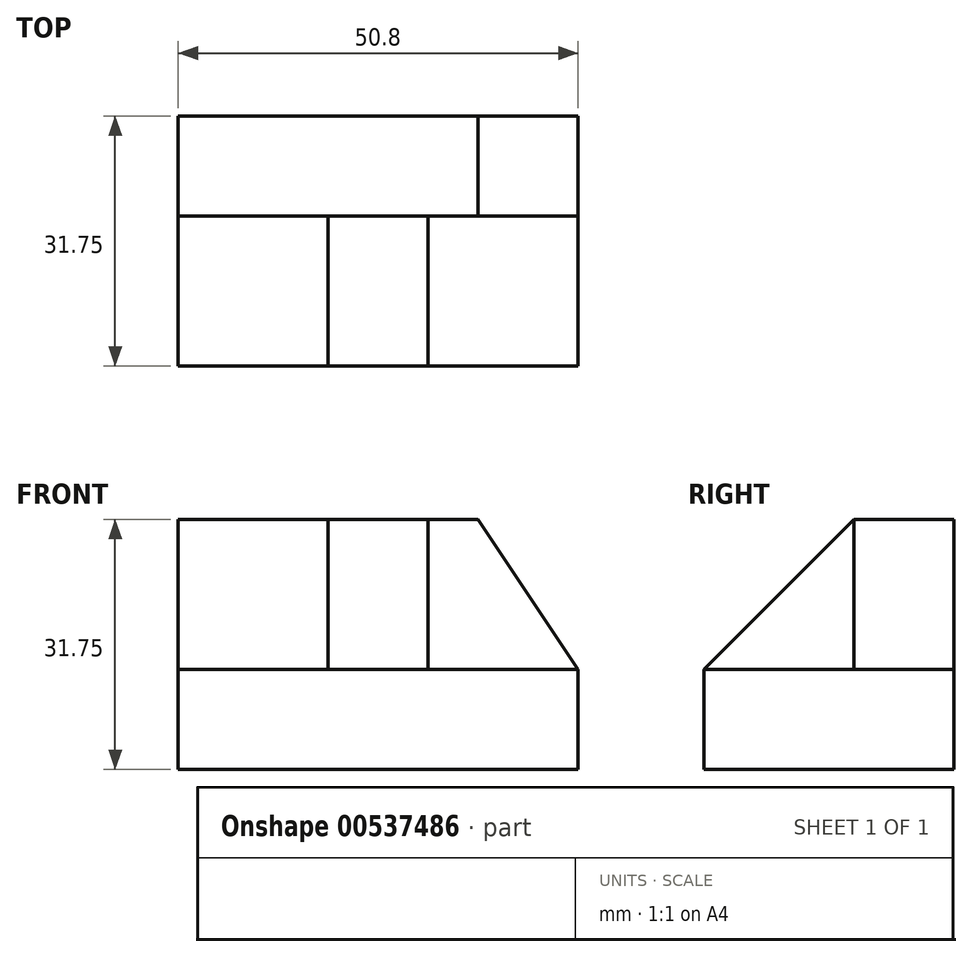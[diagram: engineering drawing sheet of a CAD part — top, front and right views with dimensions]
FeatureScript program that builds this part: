
annotation { "Feature Type Name" : "Feature", "Feature Type Description" : "" }
export const myFeature = defineFeature(function(context is Context, id is Id, definition is map)
    precondition{}
    {
        {
            var Q0;
            Q0=qCreatedBy(makeId("Front.planeOp"),FACE);
            var sketch = newSketch(context, id + "F0", { "sketchPlane" : qUnion([Q0])});
            skLineSegment(sketch, "E0", {"start": v(0, 0) * mm, "end": v(50.8, 0) * mm});
            skLineSegment(sketch, "E1", {"start": v(50.8, 0) * mm, "end": v(50.8, 31.75) * mm});
            skLineSegment(sketch, "E2", {"start": v(50.8, 31.75) * mm, "end": v(0, 31.75) * mm});
            skLineSegment(sketch, "E3", {"start": v(0, 31.75) * mm, "end": v(0, 0) * mm});
            skSolve(sketch);
        }
        {
            var Q0;
            Q0=makeQuery(id+"F0.imprint","IMPRINT",FACE,{"disambiguationData":[TD([[makeQuery(id+"F0.imprint","IMPRINT",EDGE,{"derivedFrom":sQuery(id+"F0.wireOp",EDGE,"E0")}),1.0]])]});
            extrude(context, id + "F1", {"entities" : qUnion([Q0]), "depth" : 31.75 * mm, "offsetDistance" : 25.4 * mm});
        }
        {
            var Q0;
            Q0=makeQuery(id+"F1.opExtrude","SWEPT_FACE",FACE,{"disambiguationData":[OSD([sQuery(id+"F0.wireOp",EDGE,"E1")])]});
            var sketch = newSketch(context, id + "F2", { "sketchPlane" : qUnion([Q0])});
            skLineSegment(sketch, "E4", {"start": v(-31.75, 12.7) * mm, "end": v(-12.7, 12.7) * mm});
            skLineSegment(sketch, "E5", {"start": v(-12.7, 12.7) * mm, "end": v(-12.7, 31.75) * mm});
            skLineSegment(sketch, "E6", {"start": v(-12.7, 31.75) * mm, "end": v(-31.75, 31.75) * mm});
            skLineSegment(sketch, "E7", {"start": v(-31.75, 31.75) * mm, "end": v(-31.75, 12.7) * mm});
            skSolve(sketch);
        }
        {
            var Q0;
            Q0=makeQuery(id+"F2.imprint","IMPRINT",FACE,{"disambiguationData":[TD([[makeQuery(id+"F2.imprint","IMPRINT",EDGE,{"derivedFrom":sQuery(id+"F2.wireOp",EDGE,"E4")}),1.0]])]});
            extrude(context, id + "F3", {"entities" : qUnion([Q0]), "operationType" : NewBodyOperationType.REMOVE, "oppositeDirection" : true, "depth" : 19.05 * mm, "offsetDistance" : 25.4 * mm});
        }
        {
            var Q0;
            Q0=makeQuery(id+"F1.opExtrude","SWEPT_FACE",FACE,{"disambiguationData":[OSD([sQuery(id+"F0.wireOp",EDGE,"E3")])]});
            var sketch = newSketch(context, id + "F4", { "sketchPlane" : qUnion([Q0])});
            skLineSegment(sketch, "E8", {"start": v(31.75, 12.7) * mm, "end": v(12.7, 12.7) * mm});
            skLineSegment(sketch, "E9", {"start": v(12.7, 12.7) * mm, "end": v(12.7, 31.75) * mm});
            skLineSegment(sketch, "E10", {"start": v(12.7, 31.75) * mm, "end": v(31.75, 31.75) * mm});
            skLineSegment(sketch, "E11", {"start": v(31.75, 31.75) * mm, "end": v(31.75, 12.7) * mm});
            skSolve(sketch);
        }
        {
            var Q0;
            Q0=makeQuery(id+"F4.imprint","IMPRINT",FACE,{"disambiguationData":[TD([[makeQuery(id+"F4.imprint","IMPRINT",EDGE,{"derivedFrom":sQuery(id+"F4.wireOp",EDGE,"E8")}),-1.0]])]});
            extrude(context, id + "F5", {"entities" : qUnion([Q0]), "operationType" : NewBodyOperationType.REMOVE, "oppositeDirection" : true, "depth" : 19.05 * mm, "offsetDistance" : 25.4 * mm});
        }
        {
            var Q0;
            Q0=makeQuery(id+"F3.boolean.opBoolean","COPY",FACE,{"derivedFrom":makeQuery(id+"F3.opExtrude","CAP_FACE",FACE,{"disambiguationData":[OSD([sQuery(id+"F2.wireOp",EDGE,"E4"),sQuery(id+"F2.wireOp",EDGE,"E5"),sQuery(id+"F2.wireOp",EDGE,"E6"),sQuery(id+"F2.wireOp",EDGE,"E7")])],"isStart":false})});
            var sketch = newSketch(context, id + "F6", { "sketchPlane" : qUnion([Q0])});
            skLineSegment(sketch, "E12", {"start": v(-12.7, 31.75) * mm, "end": v(-31.75, 12.7) * mm});
            skLineSegment(sketch, "E13", {"start": v(-31.75, 12.7) * mm, "end": v(-12.7, 12.7) * mm});
            skLineSegment(sketch, "E14", {"start": v(-12.7, 12.7) * mm, "end": v(-12.7, 31.75) * mm});
            skSolve(sketch);
        }
        {
            var Q0;
            Q0=makeQuery(id+"F6.imprint","IMPRINT",FACE,{"disambiguationData":[TD([[makeQuery(id+"F6.imprint","IMPRINT",EDGE,{"derivedFrom":sQuery(id+"F6.wireOp",EDGE,"E12")}),-1.0]])]});
            extrude(context, id + "F7", {"entities" : qUnion([Q0]), "operationType" : NewBodyOperationType.REMOVE, "oppositeDirection" : true, "depth" : 12.7 * mm, "offsetDistance" : 25.4 * mm});
        }
        {
            var Q0;
            Q0=makeQuery(id+"F3.boolean.opBoolean","COPY",FACE,{"derivedFrom":makeQuery(id+"F3.opExtrude","SWEPT_FACE",FACE,{"disambiguationData":[OSD([sQuery(id+"F2.wireOp",EDGE,"E5")])]})});
            var sketch = newSketch(context, id + "F8", { "sketchPlane" : qUnion([Q0])});
            skLineSegment(sketch, "E15", {"start": v(38.1, 31.75) * mm, "end": v(50.8, 12.7) * mm});
            skLineSegment(sketch, "E16", {"start": v(50.8, 12.7) * mm, "end": v(50.8, 31.75) * mm});
            skLineSegment(sketch, "E17", {"start": v(50.8, 31.75) * mm, "end": v(38.1, 31.75) * mm});
            skSolve(sketch);
        }
        {
            var Q0;
            Q0=makeQuery(id+"F8.imprint","IMPRINT",FACE,{"disambiguationData":[TD([[makeQuery(id+"F8.imprint","IMPRINT",EDGE,{"derivedFrom":sQuery(id+"F8.wireOp",EDGE,"E15")}),1.0]])]});
            extrude(context, id + "F9", {"entities" : qUnion([Q0]), "operationType" : NewBodyOperationType.REMOVE, "oppositeDirection" : true, "depth" : 12.7 * mm, "offsetDistance" : 25.4 * mm});
        }
    });
